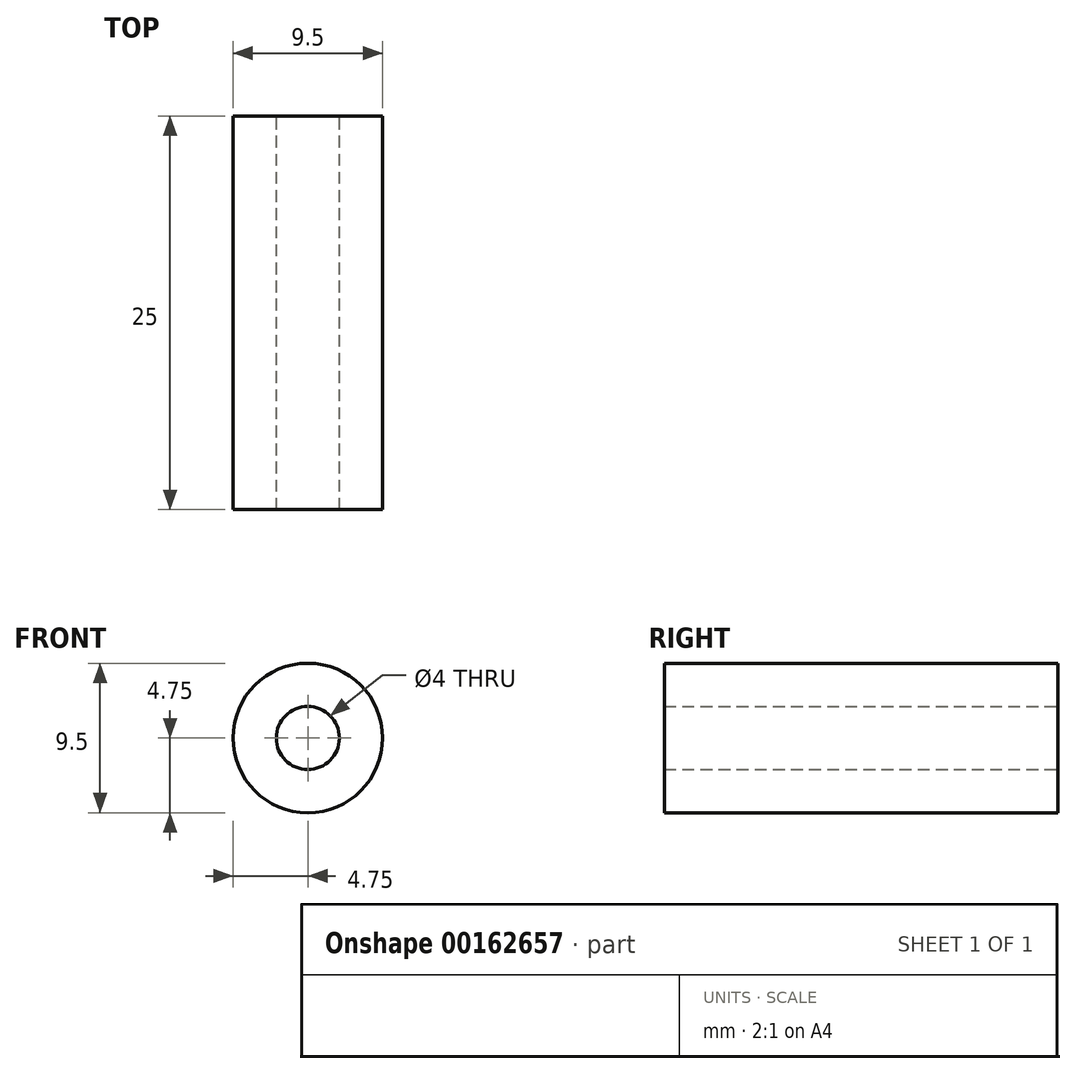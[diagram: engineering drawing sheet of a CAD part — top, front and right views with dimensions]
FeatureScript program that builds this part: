
annotation { "Feature Type Name" : "Feature", "Feature Type Description" : "" }
export const myFeature = defineFeature(function(context is Context, id is Id, definition is map)
    precondition{}
    {
        {
            var Q0;
            Q0=qCreatedBy(makeId("Front.planeOp"),FACE);
            var sketch = newSketch(context, id + "F0", { "sketchPlane" : qUnion([Q0])});
            skCircle(sketch, "E0", {"center": v(0, 0) * mm, "radius": 4.75 * mm});
            skCircle(sketch, "E1", {"center": v(0, 0) * mm, "radius": 2 * mm});
            skSolve(sketch);
        }
        {
            var Q0;
            Q0 = qSketchRegion(id + "F0", true);
            extrude(context, id + "F1", {"entities" : qUnion([Q0]), "flatOperationType" : FlatOperationType.REMOVE, "depth" : 25 * mm, "offsetDistance" : 25 * mm, "domain" : OperationDomain.MODEL});
        }
    });
